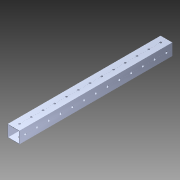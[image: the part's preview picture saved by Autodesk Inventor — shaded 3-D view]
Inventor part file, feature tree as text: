
AUTODESK INVENTOR PART (.ipt)
format: ipt  version: 2014 (Build 180170000, 170)  size: 1,342,976 bytes
history: native  units: in
note: dims shown in document units (in); Inventor stores cm internally (conversion verified against a paired STEP export)
features: extrude x2, sketch x2, pattern_circular x1, other x1, mirror x1, imported_body x1
ambient origin geometry x8: Origin, YZ Plane, XZ Plane, XY Plane, X Axis, Y Axis, Z Axis, Center Point
bodies: Body1 (feature_tree)
feature tree (8):
  pattern_circular  "CirPattern2"
  other  "1x1 tube1"
  extrude  "Extrusion1"  Depth=1.0in TaperAngle=0.0deg
  mirror  "Mirror1"
  extrude  "Extrusion2"  [1 undecoded]
  imported_body  "Base1"
  sketch  "Sketch1"  dims[d0=52.0in d1=0.0in d2=1.0in d3=0.0in]
  sketch  "Sketch4"
note: 1 required parameter value undecoded (feature->parameter linkage not recoverable at this tier; creation-order binding heuristic only, values carry confidence <= 0.55)
